# Revit family: Hager-VEGAD-Surface_mounted-IP55-With_Cover-With_DIN-Hosted-FR-fr
name_source: partatom
category: Electrical Equipment
units: mm (PartAtom-declared; Revit-internal decimal feet)

## family parameters
Cut with Voids When Loaded = No
Host = Face
Maintain Annotation Orientation = Yes
Panel Configuration = Two Columns, Circuits Across
Part Type = Panelboard
Room Calculation Point = No
Round Connector Dimension = Use Diameter
Shared = No

## types (6) — shared parameters
BC_MODEL_ID = 1547017
BC_OBJECT_ID = 513440
BC_OBJECT_VERSION = #3
Code hager = ADD-EC000214_EU
EF000003 - mode de pose = saillie
EF000007 - couleur = blanc
EF000008 - largeur = 550 mm  [stored 1.80446 ft]
EF000024 - résistant aux UV = No
EF000049 - profondeur = 275 mm  [stored 0.902231 ft]
EF000116 - numéro RAL = 9010
EF000118 - avec cadre/support de montage = No
EF001062 - finition CEM = No
EF001088 - possibilité de montage en saillie = Yes
EF001134 - rail DIN = Yes
EF002950 - largeur en nombre de modules = 24
EF004462 - type de fermeture = autre
EF005474 - indice de protection (IP) = IP55
EF006244 - couvercle/porte transparent(e) = No
EF006306 - avec serrure = No
EF009212 - finition du couvercle = fermé
EF015776 - borne de mise à la terre = Yes
EF015777 - borne à conducteur neutre = No
EF015941 - porte pour transmission du signal = No
ETIM class code = EC000214
ETIM class name = Small distribution board
HG000002-avec porte = Yes
HG000003-Gamme = VEGAD
HG000005-Epaisseur = 2 mm  [stored 0.00656168 ft]
HG000006-Encastré = No
HG000009-Porte à double battant = No
HG000010-Portes asymétriques = No
HG000011-Rangées du bas vides = No
HG000012-Angle de pivotement de la porte = 90.00°
HG000013-Porte à gauche = No
HG000014-Porte à droite = Yes
HG000015-Visibilité de l'emprise de la porte = Yes
HG000016-Visibilité de la porte 3D = Yes
HG000017-Distance entre pôles = 18 mm  [stored 0.0590551 ft]
HG000060-RAL-number = 9010
HG000099-ID modèle Onfly = 507532
HGEF0002950-largeur en nombre de modules = 24
Manufacturer = Hager
Name = VEGAD-Surface_mounted-IP55-With_Cover-With_DIN-FR
Name BIM&CO = Electricity
Name hager = ADD_Enclosures_EC000214
Uniformat = Low Tension Service & Dist.
Uniformat code = D501001
zero-valued in all types: Default Elevation, EF000218 - profondeur d'encastrement, EF000332 - hauteur d'encastrement, EF000846 - largeur d'encastrement, EF001131 - profondeur intérieure, HG000007-Nombre de colonnes vides

## per-type parameters (varying)
| type | BC_VARIANT_ID | EF000040 - hauteur | EF000266 - nombre de rangées | HG000001-nombre de colonnes | HG000004-Référence fabricant | HG000008-Nombre de rangées vides | HGEF000266-Nombre de rangées |
| VEGAD-Surface_mounted_W550_H500_D275_24_Modular_Spacing-FV22A | 1173928 | 500 mm  [stored 1.64042 ft] | 0 | 0 | FV22A | 0 | 0 |
| VEGAD-Surface_mounted_W550_H650_D275_24_Modular_Spacing-FV32A | 1173931 | 650 mm  [stored 2.13255 ft] | 3 | 1 | FV32A | 2 | 3 |
| VEGAD-Surface_mounted_W550_H800_D275_24_Modular_Spacing-FV42A | 1173933 | 800 mm  [stored 2.62467 ft] | 4 | 1 | FV42A | 2 | 4 |
| VEGAD-Surface_mounted_W550_H950_D275_24_Modular_Spacing-FV52A | 1173935 | 950 mm  [stored 3.1168 ft] | 5 | 1 | FV52A | 2 | 5 |
| VEGAD-Surface_mounted_W550_H1100_D275_24_Modular_Spacing-FV62A | 1173937 | 1100 mm | 6 | 1 | FV62A | 2 | 6 |
| VEGAD-Surface_mounted_W550_H1250_D275_24_Modular_Spacing-FV72A | 1173940 | 1250 mm  [stored 4.10105 ft] | 7 | 1 | FV72A | 2 | 7 |

note: column(s) folded — value = type name in every type: Reference

note: [stored X ft] marks values corroborated as IEEE doubles in the binary element streams (Revit-internal decimal feet)

## geometry (parser evidence)
native form markers: Sweep x15
no freeform markers — native parametric forms only
